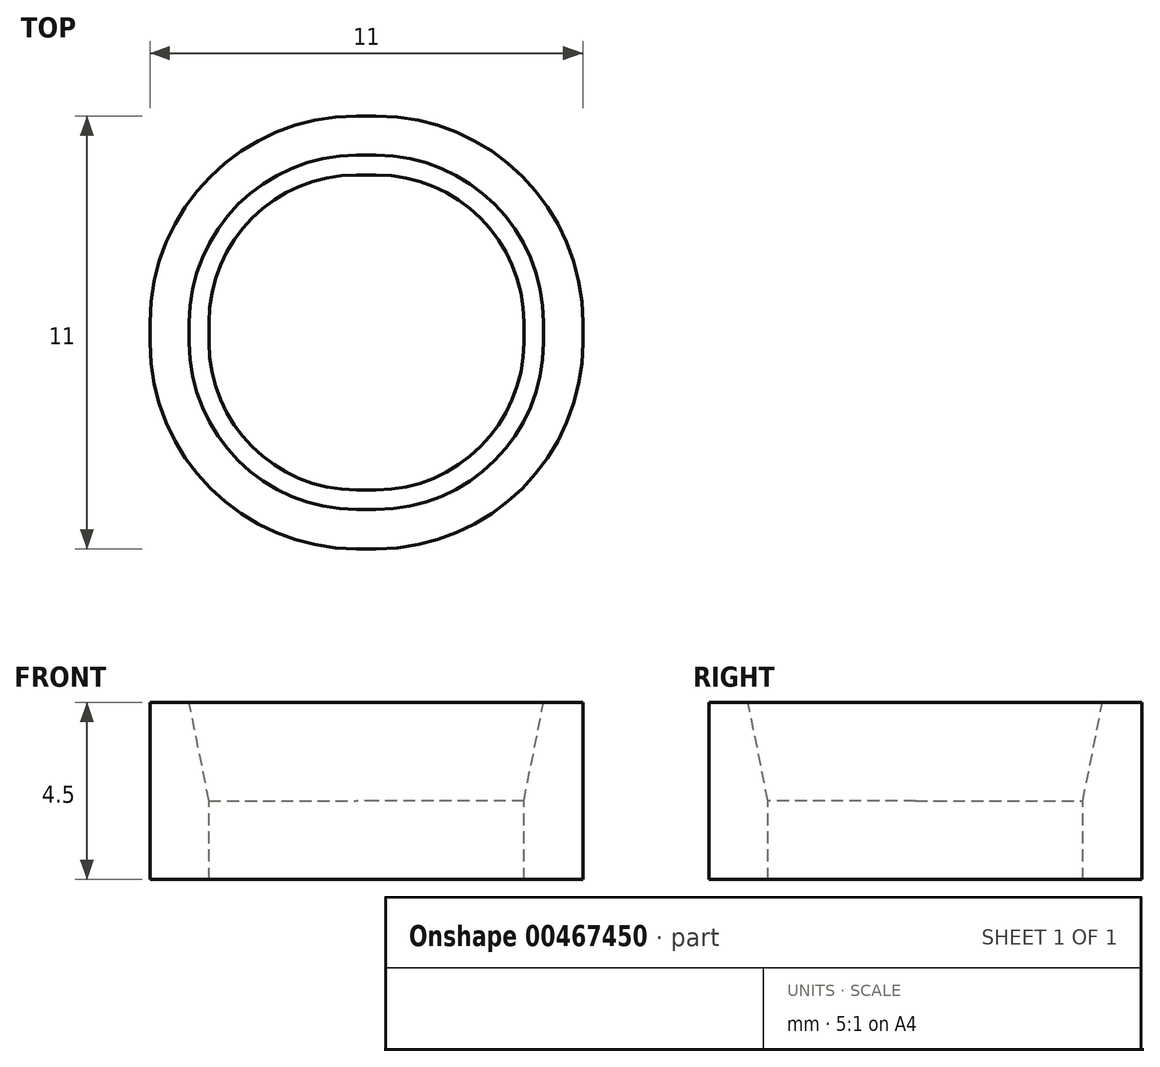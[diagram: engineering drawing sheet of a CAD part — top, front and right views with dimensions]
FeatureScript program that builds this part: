
annotation { "Feature Type Name" : "Feature", "Feature Type Description" : "" }
export const myFeature = defineFeature(function(context is Context, id is Id, definition is map)
    precondition{}
    {
        {
            var Q0;
            Q0=qCreatedBy(makeId("Right.planeOp"),FACE);
            var sketch = newSketch(context, id + "F0", { "sketchPlane" : qUnion([Q0])});
            skLineSegment(sketch, "E0", {"start": v(3.25, 0) * mm, "end": v(4.25, 5) * mm});
            skLineSegment(sketch, "E1", {"start": v(4.25, 5) * mm, "end": v(5.25, 5) * mm});
            skLineSegment(sketch, "E2", {"start": v(5.25, 5) * mm, "end": v(5.25, 0) * mm});
            skLineSegment(sketch, "E3", {"start": v(5.25, 0) * mm, "end": v(3.25, 0) * mm});
            skLineSegment(sketch, "E4", {"start": v(0, 0) * mm, "end": v(0, 5) * mm, "construction": true});
            skLineSegment(sketch, "E5", {"start": v(3.75, 2.5) * mm, "end": v(5.25, 2.5) * mm});
            skSolve(sketch);
        }
        {
            var Q0;
            {var subQ0=sQuery(id+"F0.wireOp",EDGE,"E1");Q0=makeQuery(id+"F0.imprint","IMPRINT",FACE,{"disambiguationData":[TD([[makeQuery(id+"F0.imprint","IMPRINT",EDGE,{"derivedFrom":subQ0}),-1.0]])]});}
            var Q1;
            Q1=sQuery(id+"F0.wireOp",EDGE,"E4");
            revolve(context, id + "F1", {"entities" : qUnion([Q0]), "axis" : qUnion([Q1]), "revolveType" : RevolveType.ONE_DIRECTION, "angle" : 90 * degree});
        }
        {
            var Q0;
            Q0=makeQuery(id+"F1.opRevolve","SWEPT_FACE",FACE,{"disambiguationData":[OSD([sQuery(id+"F0.wireOp",EDGE,"E5")])]});
            extrude(context, id + "F2", {"entities" : qUnion([Q0]), "operationType" : NewBodyOperationType.ADD, "depth" : 2 * mm, "offsetDistance" : 25 * mm});
        }
        {
            var Q0;
            {var subQ0=sQuery(id+"F0.wireOp",EDGE,"E5");Q0=makeQuery(id+"F2.boolean.opBoolean","MERGE",FACE,{"derivedFrom":[makeQuery(id+"F1.opRevolve","CAP_FACE",FACE,{"disambiguationData":[OSD([sQuery(id+"F0.wireOp",EDGE,"E0"),sQuery(id+"F0.wireOp",EDGE,"E1"),sQuery(id+"F0.wireOp",EDGE,"E2"),subQ0])],"isStart":true}),makeQuery(id+"F2.opExtrude","SWEPT_FACE",FACE,{"disambiguationData":[OSD([subQ0]),TDD([makeQuery(id+"F1.opRevolve","CAP_EDGE",EDGE,{"disambiguationData":[OSD([subQ0])],"isStart":true})])]})]});}
            extrude(context, id + "F3", {"entities" : qUnion([Q0]), "operationType" : NewBodyOperationType.ADD, "depth" : .25 * mm, "offsetDistance" : 25 * mm});
        }
        {
            var Q0;
            {var subQ0=sQuery(id+"F0.wireOp",EDGE,"E5");Q0=makeQuery(id+"F2.boolean.opBoolean","MERGE",FACE,{"derivedFrom":[makeQuery(id+"F1.opRevolve","CAP_FACE",FACE,{"disambiguationData":[OSD([sQuery(id+"F0.wireOp",EDGE,"E0"),sQuery(id+"F0.wireOp",EDGE,"E1"),sQuery(id+"F0.wireOp",EDGE,"E2"),subQ0])],"isStart":false}),makeQuery(id+"F2.opExtrude","SWEPT_FACE",FACE,{"disambiguationData":[OSD([subQ0]),TDD([makeQuery(id+"F1.opRevolve","CAP_EDGE",EDGE,{"disambiguationData":[OSD([subQ0])],"isStart":false})])]})]});}
            extrude(context, id + "F4", {"entities" : qUnion([Q0]), "operationType" : NewBodyOperationType.ADD, "depth" : .25 * mm, "offsetDistance" : 25 * mm});
        }
        {
            var Q0;
            Q0=makeQuery(id+"F1.opRevolve","SWEPT_BODY",BODY,{"disambiguationData":[OSD([sQuery(id+"F0.wireOp",EDGE,"E0"),sQuery(id+"F0.wireOp",EDGE,"E1"),sQuery(id+"F0.wireOp",EDGE,"E2"),sQuery(id+"F0.wireOp",EDGE,"E5")])]});
            var Q1;
            Q1=makeQuery(id+"F4.opExtrude","CAP_FACE",FACE,{"disambiguationData":[OSD([sQuery(id+"F0.wireOp",EDGE,"E0"),sQuery(id+"F0.wireOp",EDGE,"E1"),sQuery(id+"F0.wireOp",EDGE,"E2"),sQuery(id+"F0.wireOp",EDGE,"E5")])],"isStart":false});
            mirror(context, id + "F5", {"operationType" : NewBodyOperationType.ADD, "entities" : qUnion([Q0]), "mirrorPlane" : qUnion([Q1])});
        }
        {
            var Q0;
            Q0=makeQuery(id+"F1.opRevolve","SWEPT_BODY",BODY,{"disambiguationData":[OSD([sQuery(id+"F0.wireOp",EDGE,"E0"),sQuery(id+"F0.wireOp",EDGE,"E1"),sQuery(id+"F0.wireOp",EDGE,"E2"),sQuery(id+"F0.wireOp",EDGE,"E5")])]});
            var Q1;
            Q1=makeQuery(id+"F5.opPattern","COPY",FACE,{"derivedFrom":makeQuery(id+"F3.opExtrude","CAP_FACE",FACE,{"disambiguationData":[OSD([sQuery(id+"F0.wireOp",EDGE,"E0"),sQuery(id+"F0.wireOp",EDGE,"E1"),sQuery(id+"F0.wireOp",EDGE,"E2"),sQuery(id+"F0.wireOp",EDGE,"E5")])],"isStart":false}),"instanceName":"1"});
            mirror(context, id + "F6", {"operationType" : NewBodyOperationType.ADD, "entities" : qUnion([Q0]), "mirrorPlane" : qUnion([Q1])});
        }
    });
